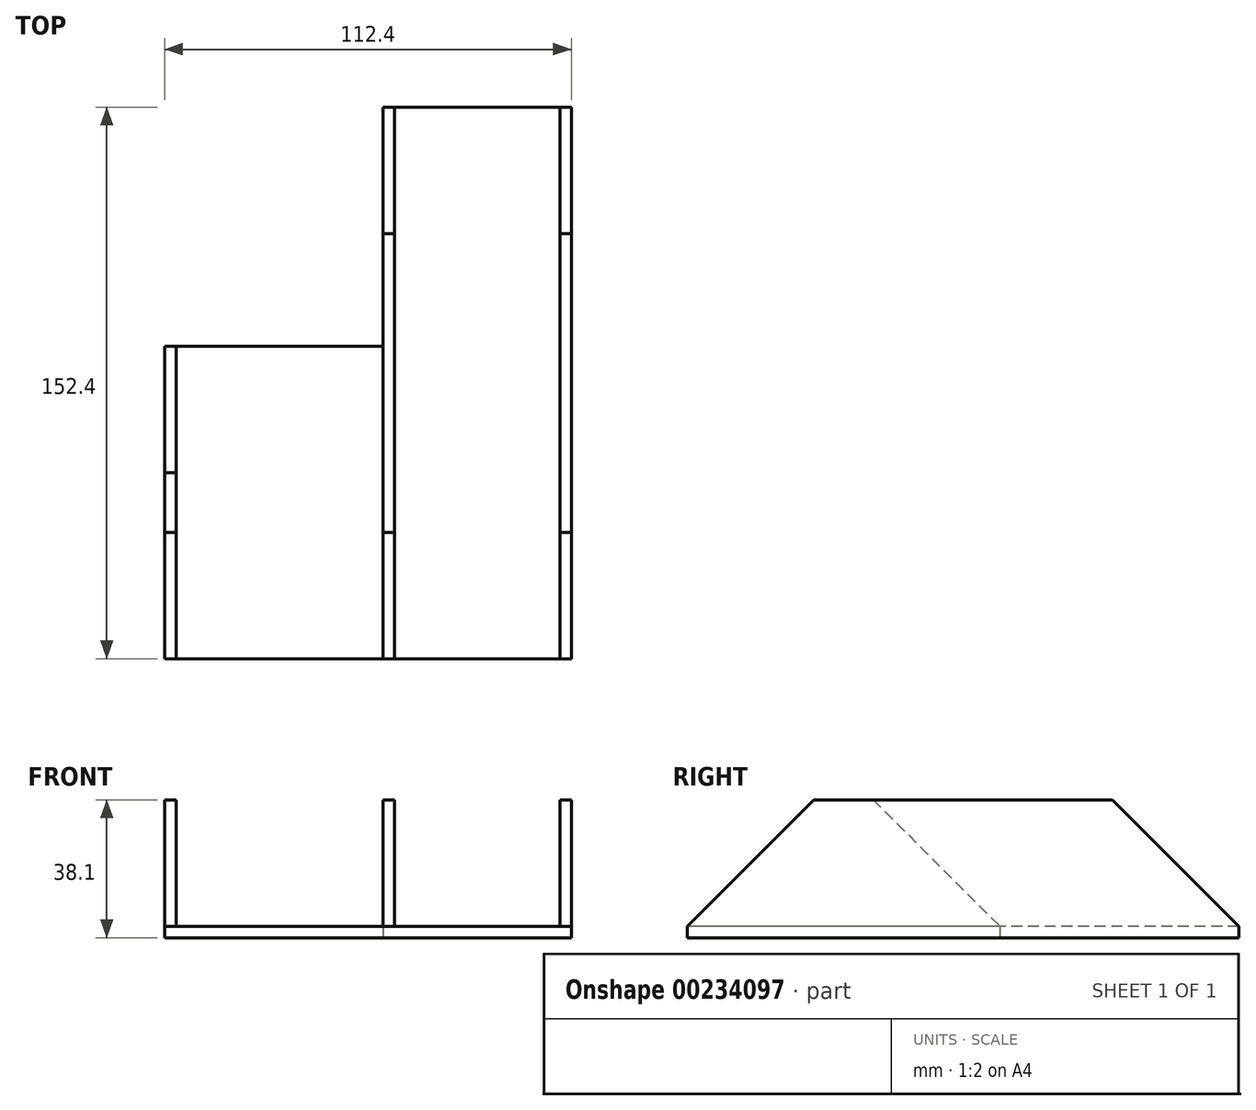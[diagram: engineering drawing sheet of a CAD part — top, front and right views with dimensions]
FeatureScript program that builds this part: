
annotation { "Feature Type Name" : "Feature", "Feature Type Description" : "" }
export const myFeature = defineFeature(function(context is Context, id is Id, definition is map)
    precondition{}
    {
        {
            var Q0;
            Q0=qCreatedBy(makeId("Top.planeOp"),FACE);
            var sketch = newSketch(context, id + "F0", { "sketchPlane" : qUnion([Q0])});
            skLineSegment(sketch, "E0.bottom", {"start": v(0, 0) * mm, "end": v(45.72, 0) * mm});
            skLineSegment(sketch, "E0.top", {"start": v(0, -152.4) * mm, "end": v(45.72, -152.4) * mm});
            skLineSegment(sketch, "E0.left", {"start": v(0, 0) * mm, "end": v(0, -152.4) * mm});
            skLineSegment(sketch, "E0.right", {"start": v(45.72, 0) * mm, "end": v(45.72, -152.4) * mm});
            skSolve(sketch);
        }
        {
            var Q0;
            Q0 = qSketchRegion(id + "F0", true);
            extrude(context, id + "F1", {"entities" : qUnion([Q0]), "depth" : 3.17 * mm});
        }
        {
            var Q0;
            Q0=makeQuery(id+"F1.opExtrude","SWEPT_FACE",FACE,{"disambiguationData":[OSD([sQuery(id+"F0.wireOp",EDGE,"E0.right")])]});
            var sketch = newSketch(context, id + "F2", { "sketchPlane" : qUnion([Q0])});
            skLineSegment(sketch, "E1", {"start": v(-152.4, 0) * mm, "end": v(-152.4, 3.18) * mm});
            skLineSegment(sketch, "E2", {"start": v(-152.4, 3.18) * mm, "end": v(-117.48, 38.1) * mm});
            skLineSegment(sketch, "E3", {"start": v(-117.48, 38.1) * mm, "end": v(-34.93, 38.1) * mm});
            skLineSegment(sketch, "E4", {"start": v(-34.93, 38.1) * mm, "end": v(0, 3.18) * mm});
            skLineSegment(sketch, "E5", {"start": v(0, 3.17) * mm, "end": v(0, 0) * mm});
            skLineSegment(sketch, "E6", {"start": v(0, 0) * mm, "end": v(-152.4, 0) * mm});
            skSolve(sketch);
        }
        {
            var Q0;
            Q0 = qSketchRegion(id + "F2", true);
            extrude(context, id + "F3", {"entities" : qUnion([Q0]), "operationType" : NewBodyOperationType.ADD, "depth" : 3.17 * mm});
        }
        {
            var Q0;
            Q0=makeQuery(id+"F1.opExtrude","SWEPT_FACE",FACE,{"disambiguationData":[OSD([sQuery(id+"F0.wireOp",EDGE,"E0.left")])]});
            var sketch = newSketch(context, id + "F4", { "sketchPlane" : qUnion([Q0])});
            skLineSegment(sketch, "E7", {"start": v(0, 0) * mm, "end": v(0, 3.18) * mm});
            skLineSegment(sketch, "E8", {"start": v(0, 3.17) * mm, "end": v(34.92, 38.1) * mm});
            skLineSegment(sketch, "E9", {"start": v(34.92, 38.1) * mm, "end": v(117.48, 38.1) * mm});
            skLineSegment(sketch, "E10", {"start": v(117.48, 38.1) * mm, "end": v(152.4, 3.18) * mm});
            skLineSegment(sketch, "E11", {"start": v(152.4, 3.18) * mm, "end": v(152.4, 0) * mm});
            skLineSegment(sketch, "E12", {"start": v(152.4, 0) * mm, "end": v(0, 0) * mm});
            skSolve(sketch);
        }
        {
            var Q0;
            Q0=makeQuery(id+"F4.imprint","IMPRINT",FACE,{"disambiguationData":[TD([[makeQuery(id+"F4.imprint","IMPRINT",EDGE,{"derivedFrom":sQuery(id+"F4.wireOp",EDGE,"E8")}),-1.0]])]});
            var Q1;
            Q1 = qSketchRegion(id + "F4", true);
            extrude(context, id + "F5", {"entities" : qUnion([Q0, Q1]), "operationType" : NewBodyOperationType.ADD, "depth" : 3.17 * mm});
        }
        {
            var Q0;
            Q0=makeQuery(id+"F5.boolean.opBoolean","MERGE",FACE,{"derivedFrom":[makeQuery(id+"F3.boolean.opBoolean","MERGE",FACE,{"derivedFrom":[makeQuery(id+"F1.opExtrude","CAP_FACE",FACE,{"disambiguationData":[OSD([sQuery(id+"F0.wireOp",EDGE,"E0.bottom"),sQuery(id+"F0.wireOp",EDGE,"E0.top"),sQuery(id+"F0.wireOp",EDGE,"E0.left"),sQuery(id+"F0.wireOp",EDGE,"E0.right")])],"isStart":true}),makeQuery(id+"F3.opExtrude","SWEPT_FACE",FACE,{"disambiguationData":[OSD([sQuery(id+"F2.wireOp",EDGE,"E6")])]})]}),makeQuery(id+"F5.opExtrude","SWEPT_FACE",FACE,{"disambiguationData":[OSD([sQuery(id+"F4.wireOp",EDGE,"E12")])]})]});
            var sketch = newSketch(context, id + "F6", { "sketchPlane" : qUnion([Q0])});
            skLineSegment(sketch, "E13.bottom", {"start": v(-3.18, 152.4) * mm, "end": v(-60.33, 152.4) * mm});
            skLineSegment(sketch, "E13.top", {"start": v(-3.17, 66.04) * mm, "end": v(-60.32, 66.04) * mm});
            skLineSegment(sketch, "E13.left", {"start": v(-3.18, 152.4) * mm, "end": v(-3.18, 66.04) * mm});
            skLineSegment(sketch, "E13.right", {"start": v(-60.33, 152.4) * mm, "end": v(-60.32, 66.04) * mm});
            skSolve(sketch);
        }
        {
            var Q0;
            Q0=makeQuery(id+"F6.imprint","IMPRINT",FACE,{"disambiguationData":[TD([[makeQuery(id+"F6.imprint","IMPRINT",EDGE,{"derivedFrom":sQuery(id+"F6.wireOp",EDGE,"E13.bottom")}),1.0]])]});
            extrude(context, id + "F7", {"entities" : qUnion([Q0]), "operationType" : NewBodyOperationType.ADD, "oppositeDirection" : true, "depth" : 3.17 * mm});
        }
        {
            var Q0;
            Q0=makeQuery(id+"F7.opExtrude","SWEPT_FACE",FACE,{"disambiguationData":[OSD([sQuery(id+"F6.wireOp",EDGE,"E13.right")])]});
            var sketch = newSketch(context, id + "F8", { "sketchPlane" : qUnion([Q0])});
            skLineSegment(sketch, "E14", {"start": v(152.4, 0) * mm, "end": v(152.4, 3.18) * mm});
            skLineSegment(sketch, "E15", {"start": v(152.4, 3.18) * mm, "end": v(117.48, 38.1) * mm});
            skLineSegment(sketch, "E16", {"start": v(117.47, 38.1) * mm, "end": v(100.97, 38.1) * mm});
            skLineSegment(sketch, "E17", {"start": v(100.97, 38.1) * mm, "end": v(66.04, 3.17) * mm});
            skLineSegment(sketch, "E18", {"start": v(66.04, 3.17) * mm, "end": v(66.04, 0) * mm});
            skLineSegment(sketch, "E19", {"start": v(66.04, 0) * mm, "end": v(152.4, 0) * mm});
            skSolve(sketch);
        }
        {
            var Q0;
            Q0 = qSketchRegion(id + "F8", true);
            extrude(context, id + "F9", {"entities" : qUnion([Q0]), "operationType" : NewBodyOperationType.ADD, "depth" : 3.17 * mm});
        }
    });
